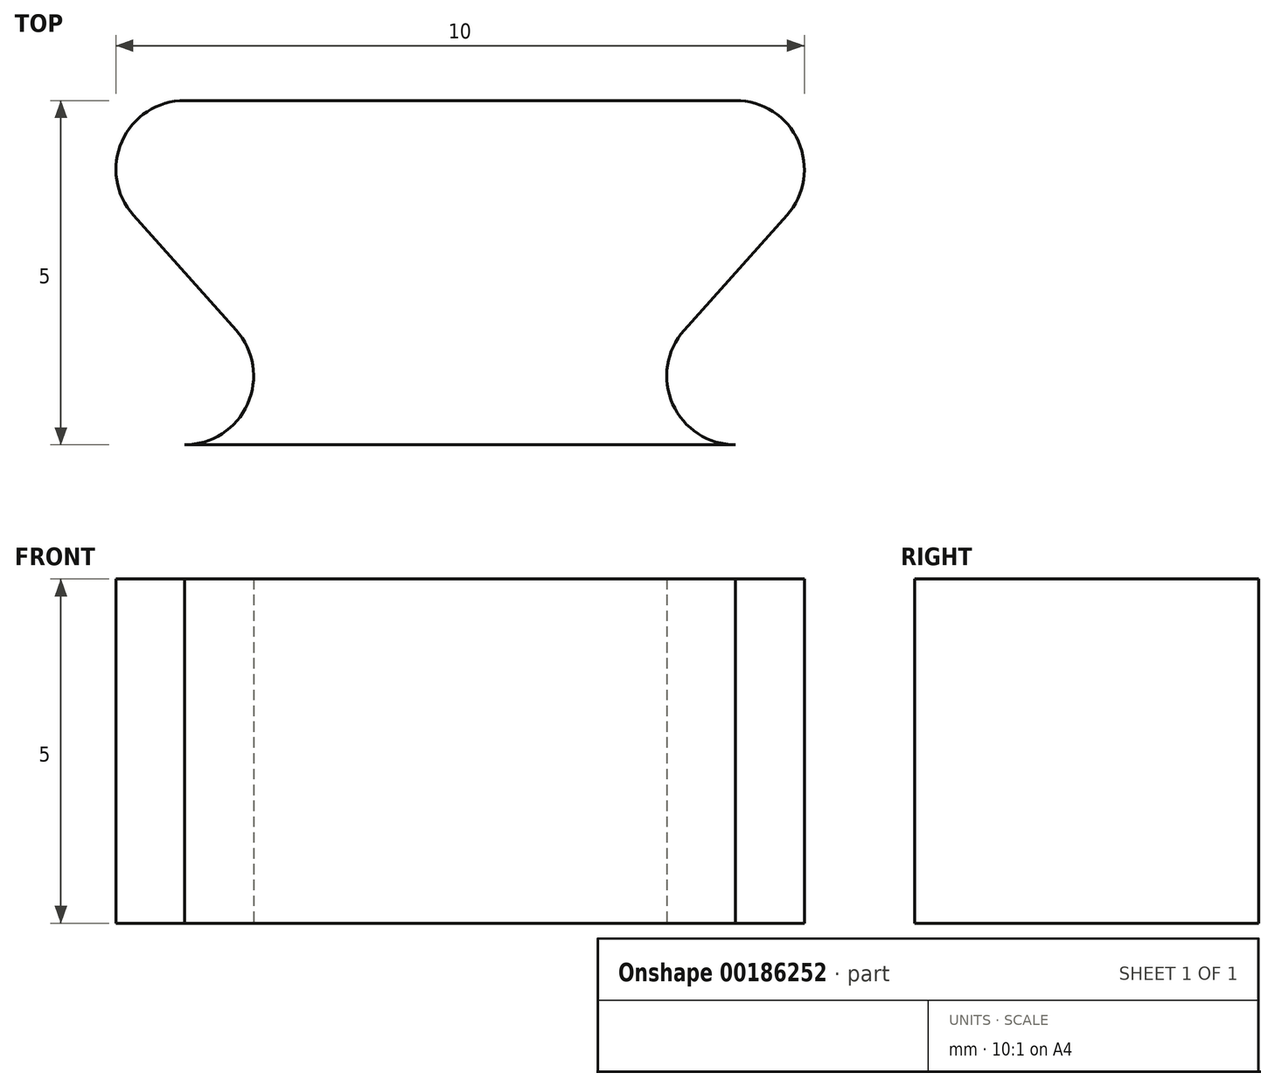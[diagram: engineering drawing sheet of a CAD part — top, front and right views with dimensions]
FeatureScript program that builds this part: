
annotation { "Feature Type Name" : "Feature", "Feature Type Description" : "" }
export const myFeature = defineFeature(function(context is Context, id is Id, definition is map)
    precondition{}
    {
        {
            var Q0;
            Q0=qCreatedBy(makeId("Top.planeOp"),FACE);
            var sketch = newSketch(context, id + "F0", { "sketchPlane" : qUnion([Q0])});
            skLineSegment(sketch, "E0", {"start": v(-4, 5) * mm, "end": v(0, 5) * mm});
            skLineSegment(sketch, "E1", {"start": v(0, 0) * mm, "end": v(-4, 0) * mm});
            skLineSegment(sketch, "E2", {"start": v(0, 0) * mm, "end": v(0, 5) * mm});
            skLineSegment(sketch, "E3", {"start": v(-3.25, 1.67) * mm, "end": v(-4.75, 3.33) * mm});
            skArc(sketch, "E4", {"start": v(-3.25, 1.67) * mm, "mid": v(-3.09, 0.6) * mm, "end": v(-4, 0) * mm});
            skArc(sketch, "E5", {"start": v(-4.75, 3.33) * mm, "mid": v(-4.91, 4.4) * mm, "end": v(-4, 5) * mm});
            skLineSegment(sketch, "E6", {"start": v(-4, 0) * mm, "end": v(-4, 5) * mm, "construction": true});
            skPoint(sketch, "E7", {"position": v(-5, 4) * mm});
            skLineSegment(sketch, "E8", {"start": v(-5, 4) * mm, "end": v(-4, 4) * mm, "construction": true});
            skSolve(sketch);
        }
        {
            var Q0;
            Q0 = qSketchRegion(id + "F0", true);
            extrude(context, id + "F1", {"entities" : qUnion([Q0]), "depth" : 5 * mm});
        }
        {
            var Q0;
            Q0=makeQuery(id+"F1.opExtrude","SWEPT_BODY",BODY,{"disambiguationData":[OSD([sQuery(id+"F0.wireOp",EDGE,"E0"),sQuery(id+"F0.wireOp",EDGE,"E1"),sQuery(id+"F0.wireOp",EDGE,"E2"),sQuery(id+"F0.wireOp",EDGE,"E3"),sQuery(id+"F0.wireOp",EDGE,"E4"),sQuery(id+"F0.wireOp",EDGE,"E5")])]});
            var Q1;
            Q1=makeQuery(id+"F1.opExtrude","SWEPT_FACE",FACE,{"disambiguationData":[OSD([sQuery(id+"F0.wireOp",EDGE,"E2")])]});
            mirror(context, id + "F2", {"operationType" : NewBodyOperationType.ADD, "entities" : qUnion([Q0]), "mirrorPlane" : qUnion([Q1])});
        }
    });
